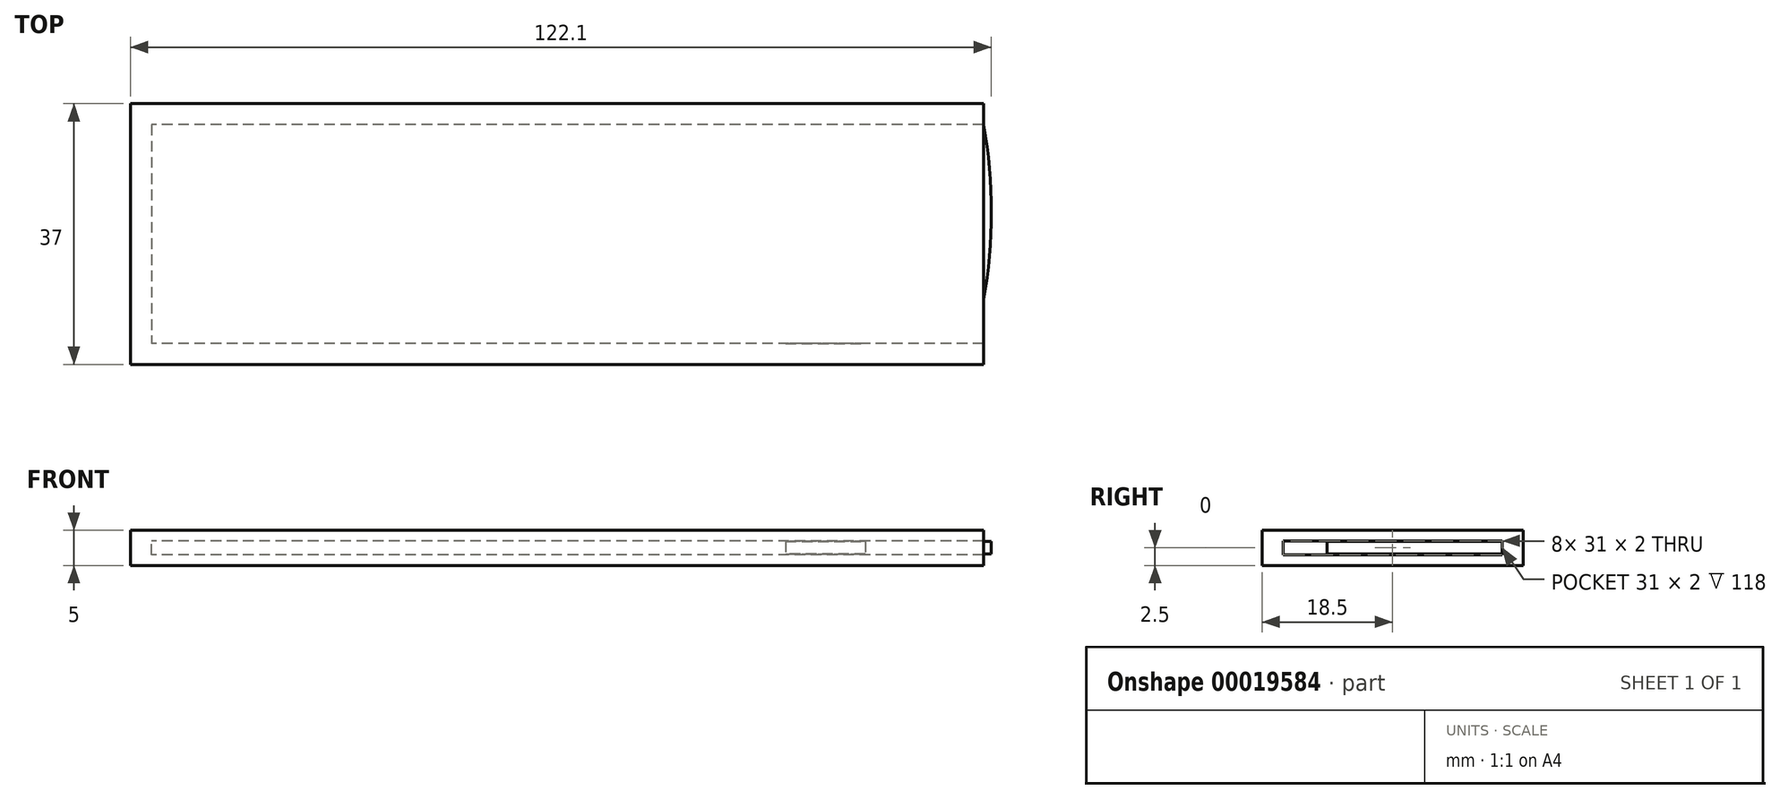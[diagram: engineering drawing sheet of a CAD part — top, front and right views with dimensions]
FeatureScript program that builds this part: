
annotation { "Feature Type Name" : "Feature", "Feature Type Description" : "" }
export const myFeature = defineFeature(function(context is Context, id is Id, definition is map)
    precondition{}
    {
        {
            var Q0;
            Q0=qCreatedBy(makeId("Top.planeOp"),FACE);
            var sketch = newSketch(context, id + "F0", { "sketchPlane" : qUnion([Q0])});
            skLineSegment(sketch, "E0", {"start": v(0, 0) * mm, "end": v(-86.68, 0) * mm});
            skArc(sketch, "E1", {"start": v(-86.68, 0) * mm, "mid": v(-105.45, -6.78) * mm, "end": v(-115.53, -24) * mm});
            skArc(sketch, "E2", {"start": v(-1.33, -30.73) * mm, "mid": v(1.04, -15.44) * mm, "end": v(0, 0) * mm});
            skArc(sketch, "E3", {"start": v(-115.53, -24) * mm, "mid": v(-113.71, -24.86) * mm, "end": v(-111.82, -25.54) * mm});
            skLineSegment(sketch, "E4", {"start": v(-115.53, -24) * mm, "end": v(0, 0) * mm, "construction": true});
            skLineSegment(sketch, "E5", {"start": v(-115.53, -24) * mm, "end": v(-1.33, -30.73) * mm, "construction": true});
            skArc(sketch, "E6", {"start": v(-109.04, -26.13) * mm, "mid": v(-55.26, -30.32) * mm, "end": v(-1.33, -30.73) * mm});
            skPoint(sketch, "E7.visualSharp", {"position": v(-110.07, -26.01) * mm});
            skArc(sketch, "E7.filletArc", {"start": v(-111.82, -25.54) * mm, "mid": v(-110.44, -25.9) * mm, "end": v(-109.04, -26.13) * mm});
            skSolve(sketch);
        }
        {
            var Q0;
            Q0 = qSketchRegion(id + "F0", true);
            extrude(context, id + "F1", {"entities" : qUnion([Q0]), "depth" : 1.78 * mm, "offsetDistance" : 25 * mm, "symmetric" : true});
        }
        {
            var Q0;
            Q0=qCreatedBy(makeId("Top.planeOp"),FACE);
            var sketch = newSketch(context, id + "F2", { "sketchPlane" : qUnion([Q0])});
            skLineSegment(sketch, "E8.bottom", {"start": v(0, 0) * mm, "end": v(-118, 0) * mm});
            skLineSegment(sketch, "E8.top", {"start": v(0, -31) * mm, "end": v(-118, -31) * mm});
            skLineSegment(sketch, "E8.left", {"start": v(0, 0) * mm, "end": v(0, -31) * mm});
            skLineSegment(sketch, "E8.right", {"start": v(-118, 0) * mm, "end": v(-118, -31) * mm});
            skLineSegment(sketch, "E9.0", {"start": v(0, -34) * mm, "end": v(-121, -34) * mm});
            skLineSegment(sketch, "E9.1", {"start": v(-121, 3) * mm, "end": v(-121, -34) * mm});
            skLineSegment(sketch, "E9.2", {"start": v(0, 3) * mm, "end": v(-121, 3) * mm});
            skLineSegment(sketch, "E10", {"start": v(0, 3) * mm, "end": v(0, 0) * mm});
            skLineSegment(sketch, "E11", {"start": v(0, -31) * mm, "end": v(0, -34) * mm});
            skSolve(sketch);
        }
        {
            var Q0;
            Q0 = qSketchRegion(id + "F2", true);
            extrude(context, id + "F3", {"entities" : qUnion([Q0]), "depth" : 5 * mm, "offsetDistance" : 25 * mm, "symmetric" : true});
        }
        {
            var Q0;
            Q0=qCreatedBy(makeId("Top.planeOp"),FACE);
            var sketch = newSketch(context, id + "F4", { "sketchPlane" : qUnion([Q0])});
            skLineSegment(sketch, "E12.0", {"start": v(-118, 0) * mm, "end": v(-118, -31) * mm});
            skLineSegment(sketch, "E13.0", {"start": v(0, 0) * mm, "end": v(-118, 0) * mm});
            skLineSegment(sketch, "E14.0", {"start": v(0, -31) * mm, "end": v(-118, -31) * mm});
            skLineSegment(sketch, "E15.0", {"start": v(0, 0) * mm, "end": v(0, -31) * mm});
            skSolve(sketch);
        }
        {
            var Q0;
            Q0 = qSketchRegion(id + "F4", true);
            extrude(context, id + "F5", {"entities" : qUnion([Q0]), "operationType" : NewBodyOperationType.REMOVE, "oppositeDirection" : true, "depth" : 2 * mm, "offsetDistance" : 25 * mm, "symmetric" : true});
        }
    });
